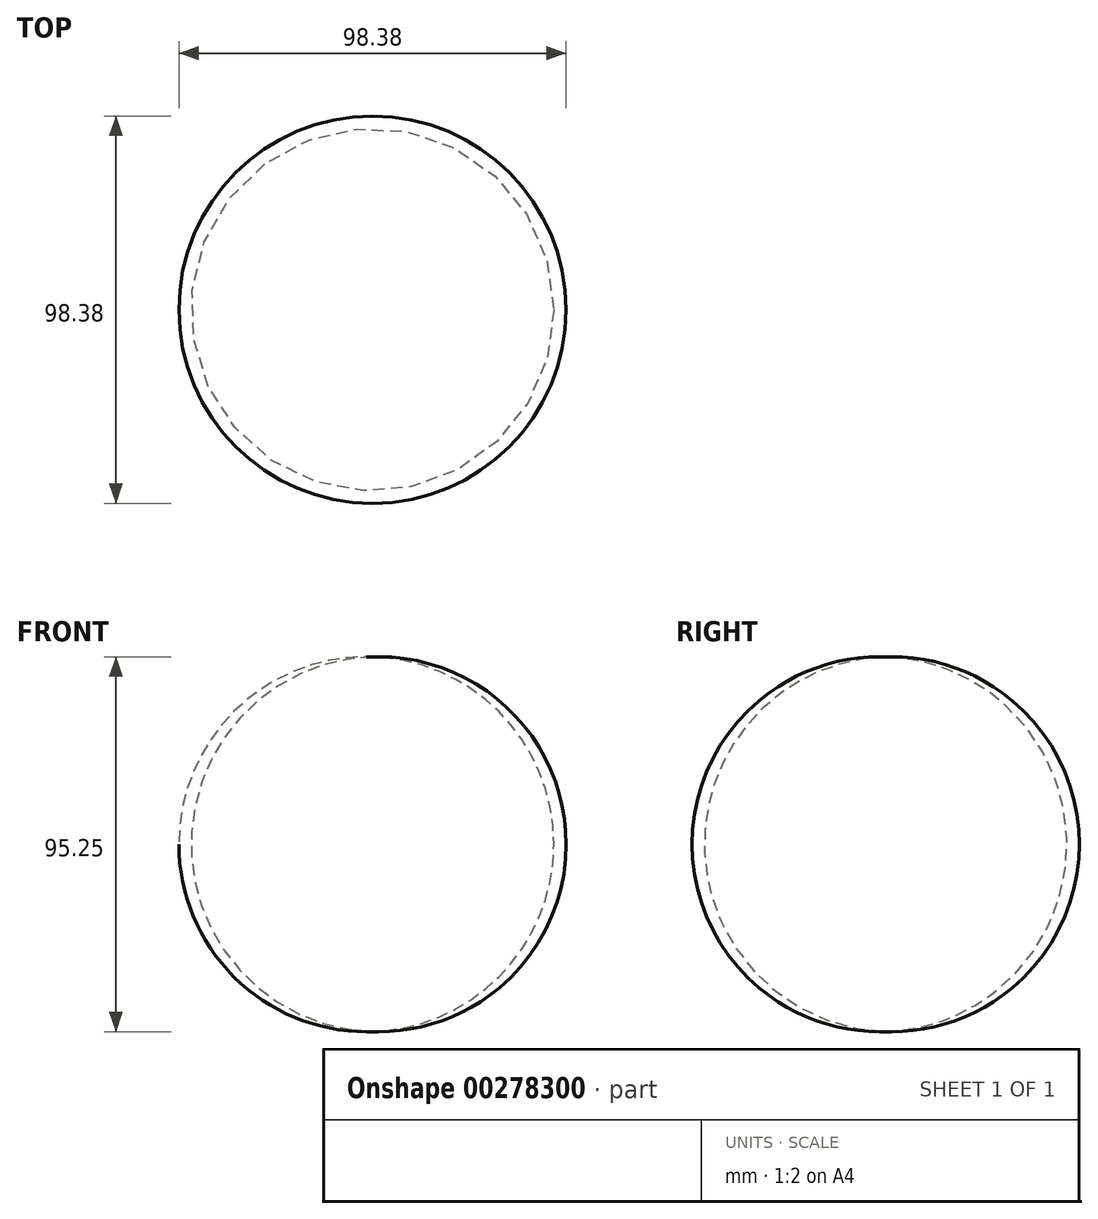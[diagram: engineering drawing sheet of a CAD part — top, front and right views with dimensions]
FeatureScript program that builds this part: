
annotation { "Feature Type Name" : "Feature", "Feature Type Description" : "" }
export const myFeature = defineFeature(function(context is Context, id is Id, definition is map)
    precondition{}
    {
        {
            var Q0;
            Q0=qCreatedBy(makeId("Right.planeOp"),FACE);
            var sketch = newSketch(context, id + "F0", { "sketchPlane" : qUnion([Q0])});
            skLineSegment(sketch, "E0", {"start": v(0, 0) * mm, "end": v(0, 47.57) * mm});
            skLineSegment(sketch, "E1", {"start": v(0, 47.57) * mm, "end": v(0, -47.63) * mm});
            skArc(sketch, "E2", {"start": v(0, -47.63) * mm, "mid": v(49.2, -0.03) * mm, "end": v(0, 47.57) * mm});
            skSolve(sketch);
        }
        {
            var Q0;
            Q0=qCreatedBy(makeId("Top.planeOp"),FACE);
            var sketch = newSketch(context, id + "F1", { "sketchPlane" : qUnion([Q0])});
            skCircle(sketch, "E3", {"center": v(0, 0) * mm, "radius": 47.63 * mm});
            skSolve(sketch);
        }
        {
            var Q0;
            {var subQ0=sQuery(id+"F0.wireOp",EDGE,"E2");Q0=makeQuery(id+"F0.imprint","IMPRINT",FACE,{"disambiguationData":[TD([[makeQuery(id+"F0.imprint","IMPRINT",EDGE,{"derivedFrom":subQ0}),1.0]])]});}
            var Q1;
            Q1=sQuery(id+"F1.wireOp",EDGE,"E3");
            revolve(context, id + "F2", {"entities" : qUnion([Q0]), "axis" : qUnion([Q1]), "revolveType" : RevolveType.FULL});
        }
    });
